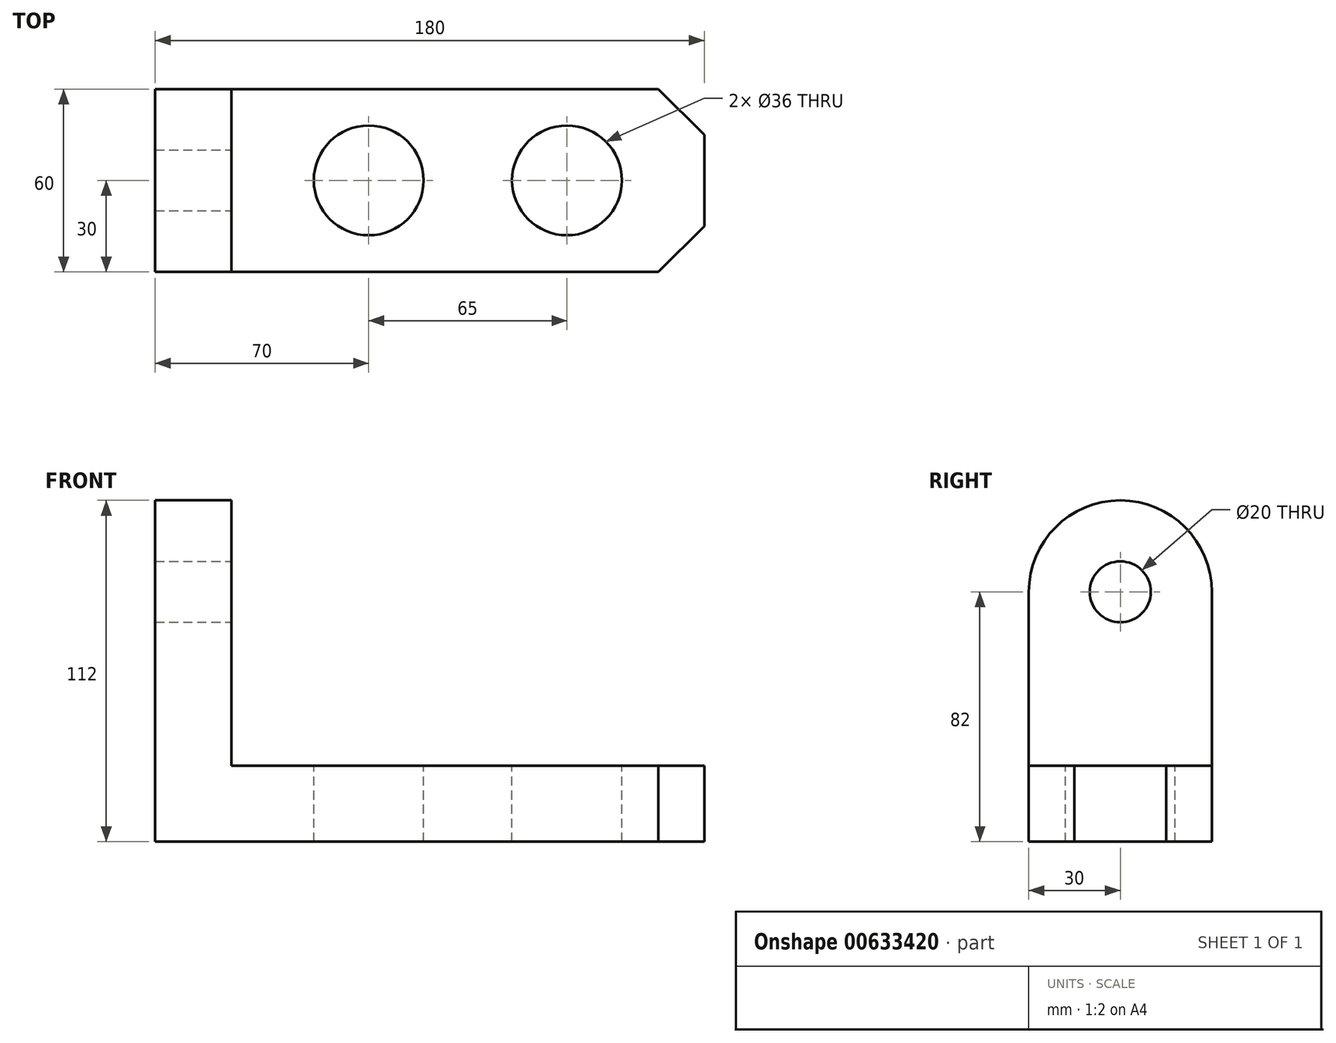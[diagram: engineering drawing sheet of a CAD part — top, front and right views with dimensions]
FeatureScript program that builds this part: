
annotation { "Feature Type Name" : "Feature", "Feature Type Description" : "" }
export const myFeature = defineFeature(function(context is Context, id is Id, definition is map)
    precondition{}
    {
        {
            var Q0;
            Q0=qCreatedBy(makeId("Top.planeOp"),FACE);
            var sketch = newSketch(context, id + "F0", { "sketchPlane" : qUnion([Q0])});
            skLineSegment(sketch, "E0.bottom", {"start": v(0, 0) * mm, "end": v(180, 0) * mm});
            skLineSegment(sketch, "E0.top", {"start": v(0, 60) * mm, "end": v(180, 60) * mm});
            skLineSegment(sketch, "E0.left", {"start": v(0, 0) * mm, "end": v(0, 60) * mm});
            skLineSegment(sketch, "E0.right", {"start": v(180, 0) * mm, "end": v(180, 60) * mm});
            skSolve(sketch);
        }
        {
            var Q0;
            Q0 = qSketchRegion(id + "F0", true);
            extrude(context, id + "F1", {"entities" : qUnion([Q0]), "depth" : 25 * mm, "offsetDistance" : 25.4 * mm});
        }
        {
            var Q0;
            Q0=makeQuery(id+"F1.opExtrude","CAP_FACE",FACE,{"disambiguationData":[OSD([sQuery(id+"F0.wireOp",EDGE,"E0.bottom"),sQuery(id+"F0.wireOp",EDGE,"E0.top"),sQuery(id+"F0.wireOp",EDGE,"E0.left"),sQuery(id+"F0.wireOp",EDGE,"E0.right")])],"isStart":false});
            var sketch = newSketch(context, id + "F2", { "sketchPlane" : qUnion([Q0])});
            skLineSegment(sketch, "E1.bottom", {"start": v(0, 60) * mm, "end": v(25, 60) * mm});
            skLineSegment(sketch, "E1.top", {"start": v(0, 0) * mm, "end": v(25, 0) * mm});
            skLineSegment(sketch, "E1.left", {"start": v(0, 60) * mm, "end": v(0, 0) * mm});
            skLineSegment(sketch, "E1.right", {"start": v(25, 60) * mm, "end": v(25, 0) * mm});
            skSolve(sketch);
        }
        {
            var Q0;
            Q0 = qSketchRegion(id + "F2", true);
            extrude(context, id + "F3", {"entities" : qUnion([Q0]), "operationType" : NewBodyOperationType.ADD, "depth" : 87 * mm, "offsetDistance" : 25.4 * mm});
        }
        {
            var Q0;
            Q0=makeQuery(id+"F3.opExtrude","CAP_EDGE",EDGE,{"disambiguationData":[OSD([sQuery(id+"F2.wireOp",EDGE,"E1.top")])],"isStart":false});
            var Q1;
            Q1=makeQuery(id+"F3.opExtrude","CAP_EDGE",EDGE,{"disambiguationData":[OSD([sQuery(id+"F2.wireOp",EDGE,"E1.bottom")])],"isStart":false});
            fillet(context, id + "F4", {"entities" : qUnion([Q0, Q1]), "radius" : 30 * mm, "tangentPropagation" : true, "allowEdgeOverflow" : false});
        }
        {
            var Q0;
            Q0=makeQuery(id+"F1.opExtrude","SWEPT_EDGE",EDGE,{"disambiguationData":[OSD([sQuery(id+"F0.wireOp",EDGE,"E0.bottom"),sQuery(id+"F0.wireOp",EDGE,"E0.right")])]});
            var Q1;
            Q1=makeQuery(id+"F1.opExtrude","SWEPT_EDGE",EDGE,{"disambiguationData":[OSD([sQuery(id+"F0.wireOp",EDGE,"E0.top"),sQuery(id+"F0.wireOp",EDGE,"E0.right")])]});
            chamfer(context, id + "F5", {"entities" : qUnion([Q0, Q1]), "width" : 15 * mm, "tangentPropagation" : true});
        }
        {
            var Q0;
            {var subQ0=sQuery(id+"F2.wireOp",EDGE,"E1.right");Q0=makeQuery(id+"F2.imprint","IMPRINT",FACE,{"disambiguationData":[TD([[makeQuery(id+"F2.imprint","IMPRINT",EDGE,{"derivedFrom":subQ0}),1.0]])]});}
            var sketch = newSketch(context, id + "F6", { "sketchPlane" : qUnion([Q0])});
            skCircle(sketch, "E2", {"center": v(70, 30) * mm, "radius": 18 * mm});
            skCircle(sketch, "E3", {"center": v(135, 30) * mm, "radius": 18 * mm});
            skSolve(sketch);
        }
        {
            var Q0;
            Q0 = qSketchRegion(id + "F6", true);
            extrude(context, id + "F7", {"entities" : qUnion([Q0]), "operationType" : NewBodyOperationType.REMOVE, "oppositeDirection" : true, "depth" : 25 * mm, "offsetDistance" : 25.4 * mm});
        }
        {
            var Q0;
            Q0=makeQuery(id+"F3.opExtrude","SWEPT_FACE",FACE,{"disambiguationData":[OSD([sQuery(id+"F2.wireOp",EDGE,"E1.right")])]});
            var sketch = newSketch(context, id + "F8", { "sketchPlane" : qUnion([Q0])});
            skCircle(sketch, "E4", {"center": v(30, 82) * mm, "radius": 10 * mm});
            skSolve(sketch);
        }
        {
            var Q0;
            Q0 = qSketchRegion(id + "F8", true);
            extrude(context, id + "F9", {"entities" : qUnion([Q0]), "operationType" : NewBodyOperationType.REMOVE, "endBound" : BoundingType.THROUGH_ALL, "oppositeDirection" : true, "depth" : 25 * mm, "offsetDistance" : 25.4 * mm});
        }
    });
